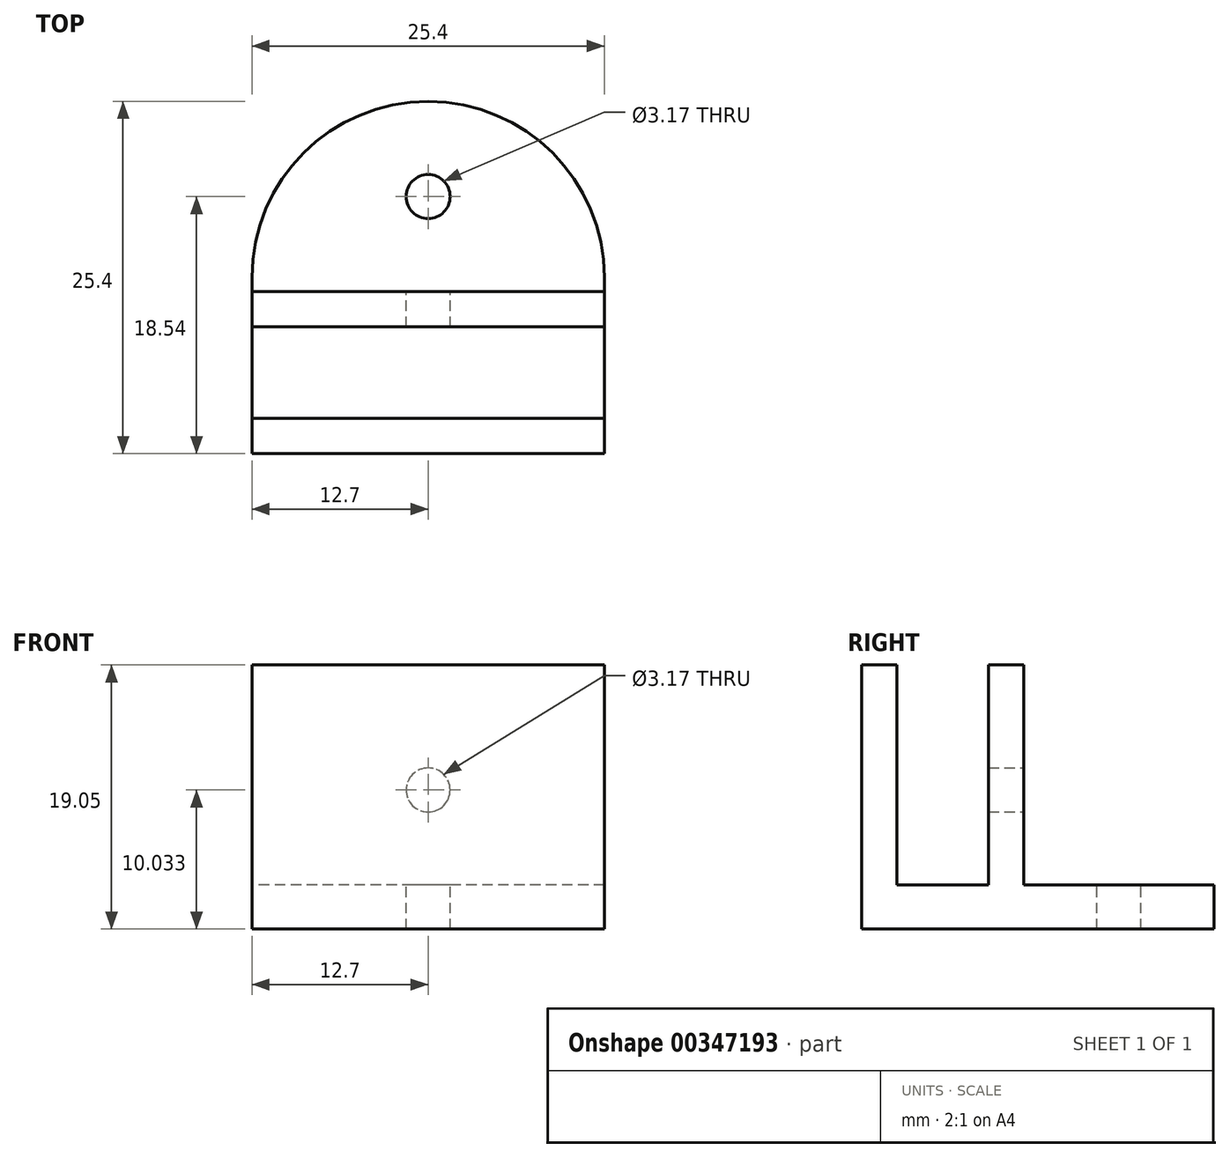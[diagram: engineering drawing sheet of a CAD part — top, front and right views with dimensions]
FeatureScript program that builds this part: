
annotation { "Feature Type Name" : "Feature", "Feature Type Description" : "" }
export const myFeature = defineFeature(function(context is Context, id is Id, definition is map)
    precondition{}
    {
        {
            var Q0;
            Q0=qCreatedBy(makeId("Top.planeOp"),FACE);
            var sketch = newSketch(context, id + "F0", { "sketchPlane" : qUnion([Q0])});
            skLineSegment(sketch, "E0.bottom", {"start": v(12.7, -5.84) * mm, "end": v(-12.7, -5.84) * mm});
            skLineSegment(sketch, "E0.top", {"start": v(12.7, 5.84) * mm, "end": v(-12.7, 5.84) * mm});
            skLineSegment(sketch, "E0.left", {"start": v(12.7, -5.84) * mm, "end": v(12.7, 5.84) * mm});
            skLineSegment(sketch, "E0.right", {"start": v(-12.7, -5.84) * mm, "end": v(-12.7, 5.84) * mm});
            skPoint(sketch, "E0.middle", {"position": v(0, 0) * mm});
            skLineSegment(sketch, "E1.bottom", {"start": v(12.7, -3.3) * mm, "end": v(-12.7, -3.3) * mm});
            skLineSegment(sketch, "E1.top", {"start": v(12.7, 3.3) * mm, "end": v(-12.7, 3.3) * mm});
            skLineSegment(sketch, "E1.left", {"start": v(12.7, -3.3) * mm, "end": v(12.7, 3.3) * mm});
            skLineSegment(sketch, "E1.right", {"start": v(-12.7, -3.3) * mm, "end": v(-12.7, 3.3) * mm});
            skLineSegment(sketch, "E2.bottom", {"start": v(-12.7, -5.84) * mm, "end": v(12.7, -5.84) * mm});
            skLineSegment(sketch, "E2.top", {"start": v(-12.7, 19.56) * mm, "end": v(12.7, 19.56) * mm});
            skLineSegment(sketch, "E2.left", {"start": v(-12.7, -5.84) * mm, "end": v(-12.7, 19.56) * mm});
            skLineSegment(sketch, "E2.right", {"start": v(12.7, -5.84) * mm, "end": v(12.7, 19.56) * mm});
            skSolve(sketch);
        }
        {
            var Q0;
            Q0=makeQuery(id+"F0.imprint","IMPRINT",FACE,{"disambiguationData":[TD([[makeQuery(id+"F0.imprint","IMPRINT",EDGE,{"derivedFrom":sQuery(id+"F0.wireOp",EDGE,"E1.bottom")}),-1.0]])]});
            var Q1;
            {var subQ0=sQuery(id+"F0.wireOp",EDGE,"E0.top");Q1=makeQuery(id+"F0.imprint","IMPRINT",FACE,{"disambiguationData":[TD([[makeQuery(id+"F0.imprint","IMPRINT",EDGE,{"derivedFrom":subQ0}),-1.0]])]});}
            extrude(context, id + "F1", {"entities" : qUnion([Q0, Q1]), "depth" : 3.17 * mm});
        }
        {
            var Q0;
            {var subQ0=sQuery(id+"F0.wireOp",EDGE,"E1.bottom");Q0=makeQuery(id+"F0.imprint","IMPRINT",FACE,{"disambiguationData":[TD([[makeQuery(id+"F0.imprint","IMPRINT",EDGE,{"derivedFrom":subQ0}),1.0]])]});}
            var Q1;
            {var subQ0=sQuery(id+"F0.wireOp",EDGE,"E0.top");Q1=makeQuery(id+"F0.imprint","IMPRINT",FACE,{"disambiguationData":[TD([[makeQuery(id+"F0.imprint","IMPRINT",EDGE,{"derivedFrom":subQ0}),1.0]])]});}
            extrude(context, id + "F2", {"entities" : qUnion([Q0, Q1]), "operationType" : NewBodyOperationType.ADD, "depth" : 19.05 * mm});
        }
        {
            var Q0;
            {var subQ0=sQuery(id+"F0.wireOp",EDGE,"E2.right");Q0=makeQuery(id+"F2.opExtrude","CAP_EDGE",EDGE,{"disambiguationData":[OSD([subQ0]),TDD([makeQuery(id+"F0.imprint","IMPRINT",EDGE,{"disambiguationData":[TD([[makeQuery(id+"F0.imprint","INTERSECT",VERTEX,{"derivedFrom":[sQuery(id+"F0.wireOp",EDGE,"E1.bottom"),subQ0]}),1.0]])],"derivedFrom":subQ0})])],"isStart":false});}
            var Q1;
            {var subQ0=sQuery(id+"F0.wireOp",EDGE,"E2.right");Q1=makeQuery(id+"F2.opExtrude","CAP_EDGE",EDGE,{"disambiguationData":[OSD([subQ0]),TDD([makeQuery(id+"F0.imprint","IMPRINT",EDGE,{"disambiguationData":[TD([[makeQuery(id+"F0.imprint","INTERSECT",VERTEX,{"derivedFrom":[sQuery(id+"F0.wireOp",EDGE,"E0.top"),subQ0]}),1.0]])],"derivedFrom":subQ0})])],"isStart":false});}
            var Q2;
            {var subQ0=sQuery(id+"F0.wireOp",EDGE,"E2.left");Q2=makeQuery(id+"F2.opExtrude","CAP_EDGE",EDGE,{"disambiguationData":[OSD([subQ0]),TDD([makeQuery(id+"F0.imprint","IMPRINT",EDGE,{"disambiguationData":[TD([[makeQuery(id+"F0.imprint","INTERSECT",VERTEX,{"derivedFrom":[sQuery(id+"F0.wireOp",EDGE,"E1.bottom"),subQ0]}),1.0]])],"derivedFrom":subQ0})])],"isStart":false});}
            var Q3;
            {var subQ0=sQuery(id+"F0.wireOp",EDGE,"E2.left");Q3=makeQuery(id+"F2.opExtrude","CAP_EDGE",EDGE,{"disambiguationData":[OSD([subQ0]),TDD([makeQuery(id+"F0.imprint","IMPRINT",EDGE,{"disambiguationData":[TD([[makeQuery(id+"F0.imprint","INTERSECT",VERTEX,{"derivedFrom":[sQuery(id+"F0.wireOp",EDGE,"E0.top"),subQ0]}),1.0]])],"derivedFrom":subQ0})])],"isStart":false});}
            var Q4;
            Q4=makeQuery(id+"F1.opExtrude","SWEPT_EDGE",EDGE,{"disambiguationData":[OSD([sQuery(id+"F0.wireOp",EDGE,"E2.top"),sQuery(id+"F0.wireOp",EDGE,"E2.right")])]});
            var Q5;
            Q5=makeQuery(id+"F1.opExtrude","SWEPT_EDGE",EDGE,{"disambiguationData":[OSD([sQuery(id+"F0.wireOp",EDGE,"E2.top"),sQuery(id+"F0.wireOp",EDGE,"E2.left")])]});
            fillet(context, id + "F3", {"entities" : qUnion([Q0, Q1, Q2, Q3, Q4, Q5]), "radius" : 12.7 * mm, "tangentPropagation" : true, "allowEdgeOverflow" : false});
        }
        {
            var Q0;
            Q0=makeQuery(id+"F1.opExtrude","CAP_FACE",FACE,{"disambiguationData":[OSD([sQuery(id+"F0.wireOp",EDGE,"E0.top"),sQuery(id+"F0.wireOp",EDGE,"E2.top"),sQuery(id+"F0.wireOp",EDGE,"E2.left"),sQuery(id+"F0.wireOp",EDGE,"E2.right")])],"isStart":false});
            var sketch = newSketch(context, id + "F4", { "sketchPlane" : qUnion([Q0])});
            skCircle(sketch, "E3", {"center": v(0, 12.7) * mm, "radius": 1.59 * mm});
            skLineSegment(sketch, "E4.0", {"start": v(12.7, 5.84) * mm, "end": v(-12.7, 5.84) * mm});
            skSolve(sketch);
        }
        {
            var Q0;
            Q0=makeQuery(id+"F4.imprint","IMPRINT",FACE,{"disambiguationData":[TD([[makeQuery(id+"F4.imprint","IMPRINT",EDGE,{"derivedFrom":sQuery(id+"F4.wireOp",EDGE,"E3")}),1.0]])]});
            extrude(context, id + "F5", {"entities" : qUnion([Q0]), "operationType" : NewBodyOperationType.REMOVE, "oppositeDirection" : true, "depth" : 25.4 * mm});
        }
        {
            var Q0;
            Q0=makeQuery(id+"F2.opExtrude","SWEPT_FACE",FACE,{"disambiguationData":[OSD([sQuery(id+"F0.wireOp",EDGE,"E0.top")])]});
            var sketch = newSketch(context, id + "F6", { "sketchPlane" : qUnion([Q0])});
            skCircle(sketch, "E5", {"center": v(0, 10.03) * mm, "radius": 1.59 * mm});
            skSolve(sketch);
        }
        {
            var Q0;
            Q0=makeQuery(id+"F6.imprint","IMPRINT",FACE,{"disambiguationData":[TD([[makeQuery(id+"F6.imprint","IMPRINT",EDGE,{"derivedFrom":sQuery(id+"F6.wireOp",EDGE,"E5")}),1.0]])]});
            extrude(context, id + "F7", {"entities" : qUnion([Q0]), "operationType" : NewBodyOperationType.REMOVE, "endBound" : BoundingType.UP_TO_NEXT, "oppositeDirection" : true, "depth" : 25.4 * mm});
        }
    });
